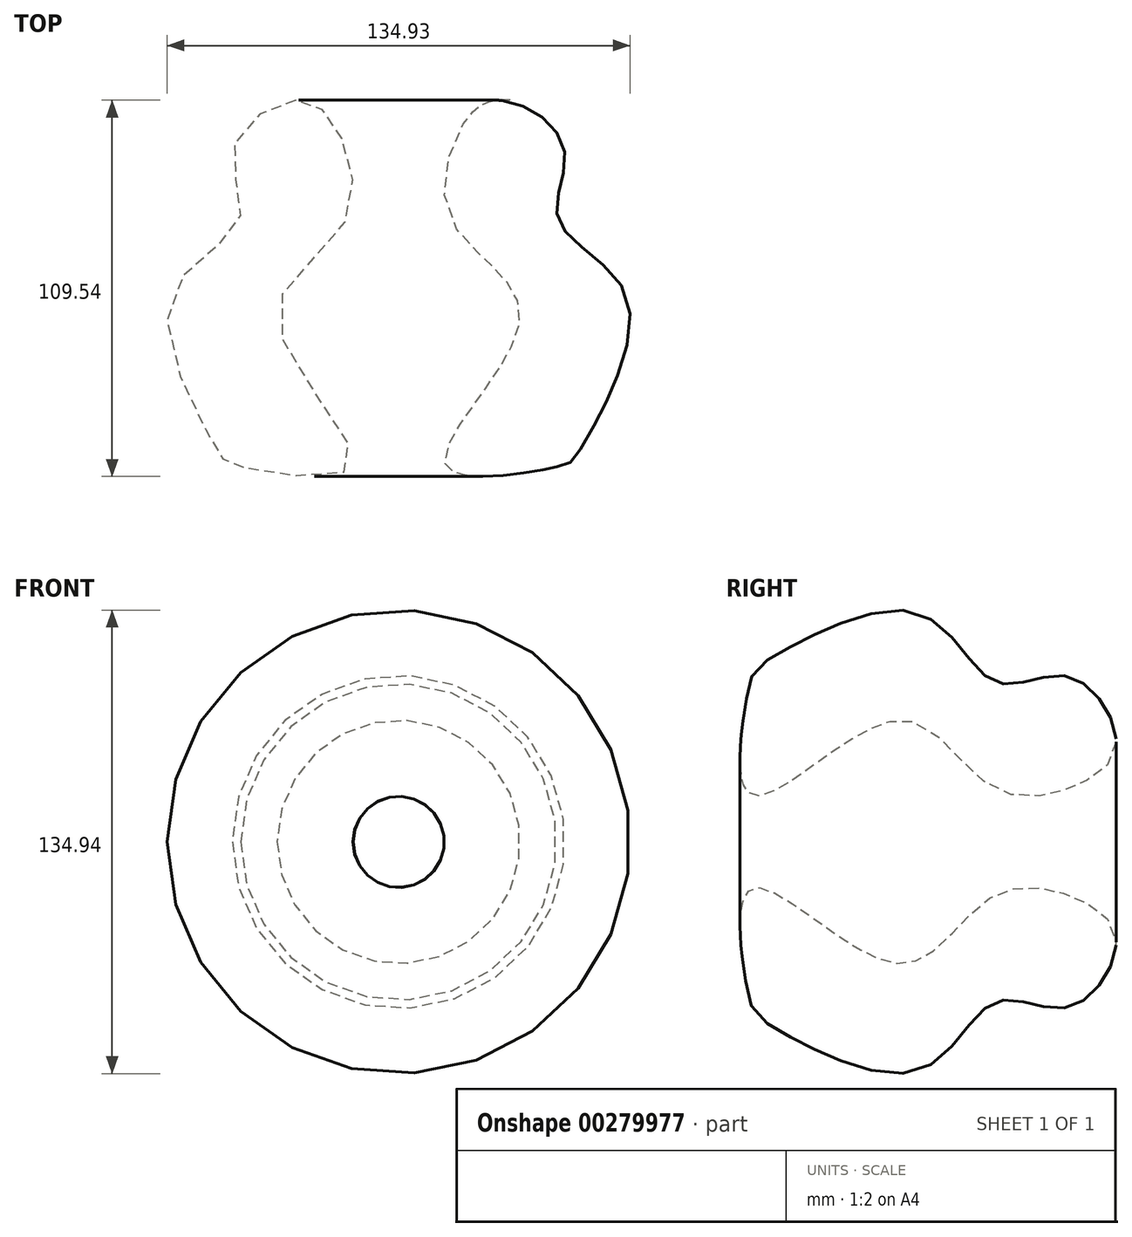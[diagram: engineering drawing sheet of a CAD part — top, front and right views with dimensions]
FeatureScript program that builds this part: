
annotation { "Feature Type Name" : "Feature", "Feature Type Description" : "" }
export const myFeature = defineFeature(function(context is Context, id is Id, definition is map)
    precondition{}
    {
        {
            var Q0;
            Q0=qCreatedBy(makeId("Top.planeOp"),FACE);
            var sketch = newSketch(context, id + "F0", { "sketchPlane" : qUnion([Q0])});
            skFitSpline(sketch, "E0", {"points": [v(-25.88, 43.63) * mm, v(-43.93, 29.98) * mm, v(-42.41, 8.5) * mm, v(-62.7, -14.96) * mm, v(-48.29, -58.82) * mm, v(-43.35, -62.7) * mm, v(-9.54, -62.73) * mm, v(-31.15, -20.3) * mm, v(-11.47, 8.07) * mm, v(-14.15, 35.93) * mm, v(-25.88, 43.63) * mm]});
            skLineSegment(sketch, "E1", {"start": v(4.2, -66.84) * mm, "end": v(4.2, 58.1) * mm});
            skSolve(sketch);
        }
        {
            var Q0;
            Q0=makeQuery(id+"F0.imprint","IMPRINT",FACE,{"disambiguationData":[TD([[makeQuery(id+"F0.imprint","IMPRINT",EDGE,{"derivedFrom":sQuery(id+"F0.wireOp",EDGE,"E0")}),1.0]])]});
            var Q1;
            Q1=sQuery(id+"F0.wireOp",EDGE,"E1");
            revolve(context, id + "F1", {"entities" : qUnion([Q0]), "axis" : qUnion([Q1]), "revolveType" : RevolveType.FULL});
        }
    });
